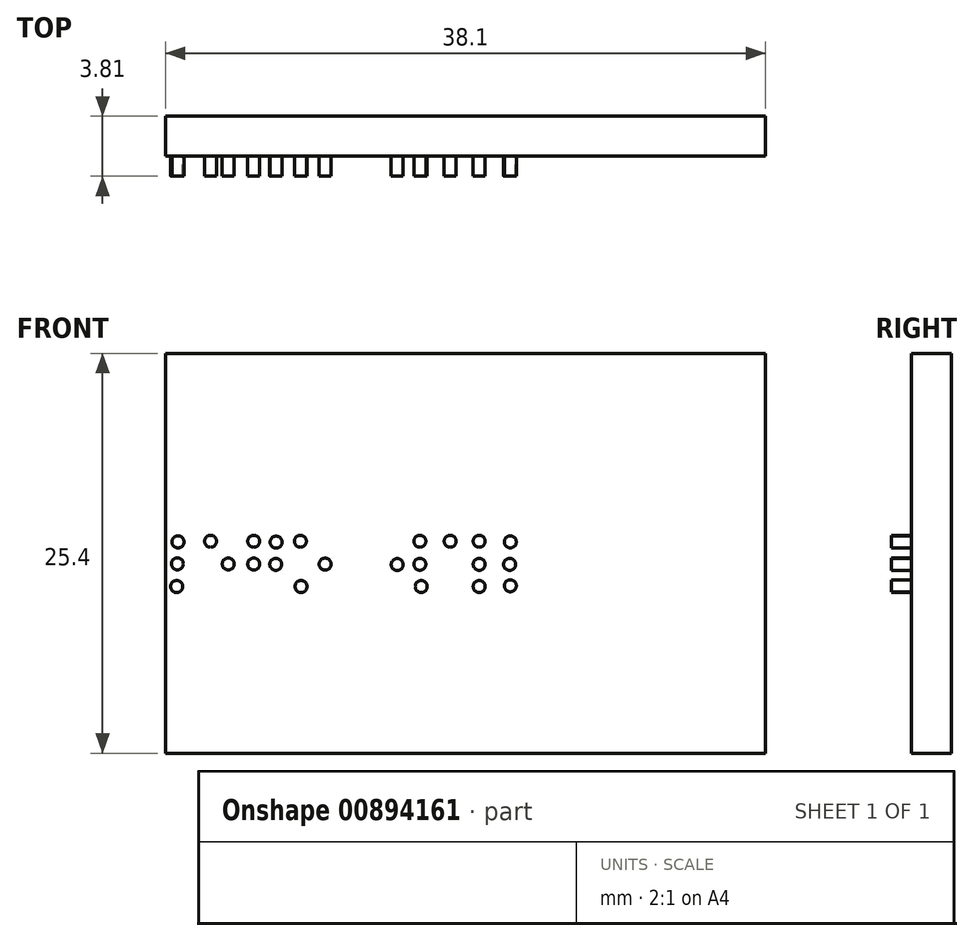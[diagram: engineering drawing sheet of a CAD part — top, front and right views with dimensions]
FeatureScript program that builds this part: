
annotation { "Feature Type Name" : "Feature", "Feature Type Description" : "" }
export const myFeature = defineFeature(function(context is Context, id is Id, definition is map)
    precondition{}
    {
        {
            var Q0;
            Q0=qCreatedBy(makeId("Front.planeOp"),FACE);
            var sketch = newSketch(context, id + "F0", { "sketchPlane" : qUnion([Q0])});
            skLineSegment(sketch, "E0.bottom", {"start": v(-23.42, 20.6) * mm, "end": v(14.68, 20.6) * mm});
            skLineSegment(sketch, "E0.top", {"start": v(-23.42, -4.8) * mm, "end": v(14.68, -4.8) * mm});
            skLineSegment(sketch, "E0.left", {"start": v(-23.42, 20.6) * mm, "end": v(-23.42, -4.8) * mm});
            skLineSegment(sketch, "E0.right", {"start": v(14.68, 20.6) * mm, "end": v(14.68, -4.8) * mm});
            skSolve(sketch);
        }
        {
            var Q0;
            Q0 = qSketchRegion(id + "F0", true);
            extrude(context, id + "F1", {"entities" : qUnion([Q0]), "depth" : 2.54 * mm, "offsetDistance" : 25.4 * mm});
        }
        {
            var Q0;
            Q0=makeQuery(id+"F1.opExtrude","CAP_FACE",FACE,{"disambiguationData":[OSD([sQuery(id+"F0.wireOp",EDGE,"E0.bottom"),sQuery(id+"F0.wireOp",EDGE,"E0.top"),sQuery(id+"F0.wireOp",EDGE,"E0.left"),sQuery(id+"F0.wireOp",EDGE,"E0.right")])],"isStart":false});
            var sketch = newSketch(context, id + "F2", { "sketchPlane" : qUnion([Q0])});
            skCircle(sketch, "E1", {"center": v(-22.63, 8.62) * mm, "radius": 0.38 * mm});
            skCircle(sketch, "E2", {"center": v(-22.67, 7.23) * mm, "radius": 0.38 * mm});
            skCircle(sketch, "E3", {"center": v(-22.72, 5.8) * mm, "radius": 0.38 * mm});
            skCircle(sketch, "E4", {"center": v(-20.56, 8.67) * mm, "radius": 0.38 * mm});
            skCircle(sketch, "E5", {"center": v(-19.44, 7.22) * mm, "radius": 0.38 * mm});
            skCircle(sketch, "E6", {"center": v(-17.82, 8.67) * mm, "radius": 0.38 * mm});
            skCircle(sketch, "E7", {"center": v(-17.82, 7.22) * mm, "radius": 0.38 * mm});
            skCircle(sketch, "E8", {"center": v(-16.42, 7.2) * mm, "radius": 0.38 * mm});
            skCircle(sketch, "E9", {"center": v(-14.86, 8.67) * mm, "radius": 0.38 * mm});
            skCircle(sketch, "E10", {"center": v(-14.82, 5.8) * mm, "radius": 0.38 * mm});
            skCircle(sketch, "E11", {"center": v(-13.29, 7.21) * mm, "radius": 0.38 * mm});
            skCircle(sketch, "E12", {"center": v(-8.7, 7.18) * mm, "radius": 0.38 * mm});
            skCircle(sketch, "E13", {"center": v(-7.27, 8.67) * mm, "radius": 0.38 * mm});
            skCircle(sketch, "E14", {"center": v(-7.27, 7.2) * mm, "radius": 0.38 * mm});
            skCircle(sketch, "E15", {"center": v(-7.18, 5.8) * mm, "radius": 0.38 * mm});
            skCircle(sketch, "E16", {"center": v(-5.34, 8.67) * mm, "radius": 0.38 * mm});
            skCircle(sketch, "E17", {"center": v(-3.5, 8.67) * mm, "radius": 0.38 * mm});
            skCircle(sketch, "E18", {"center": v(-3.5, 7.2) * mm, "radius": 0.38 * mm});
            skCircle(sketch, "E19", {"center": v(-3.5, 5.8) * mm, "radius": 0.38 * mm});
            skCircle(sketch, "E20", {"center": v(-1.52, 8.62) * mm, "radius": 0.38 * mm});
            skCircle(sketch, "E21", {"center": v(-1.57, 7.2) * mm, "radius": 0.38 * mm});
            skCircle(sketch, "E22", {"center": v(-1.52, 5.84) * mm, "radius": 0.38 * mm});
            skCircle(sketch, "E23", {"center": v(-16.4, 8.6) * mm, "radius": 0.38 * mm});
            skSolve(sketch);
        }
        {
            var Q0;
            Q0 = qSketchRegion(id + "F2", true);
            extrude(context, id + "F3", {"entities" : qUnion([Q0]), "operationType" : NewBodyOperationType.ADD, "depth" : 1.27 * mm, "offsetDistance" : 25.4 * mm});
        }
    });
